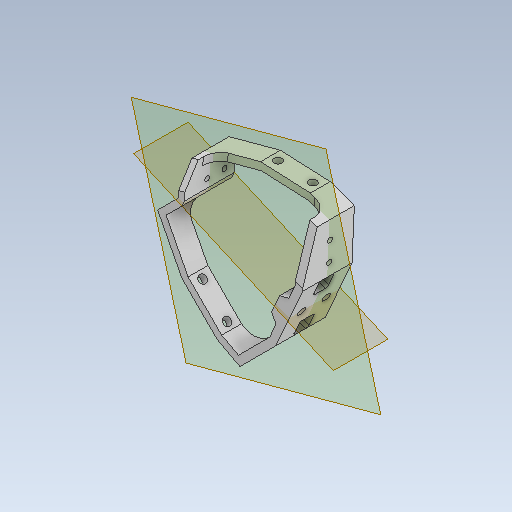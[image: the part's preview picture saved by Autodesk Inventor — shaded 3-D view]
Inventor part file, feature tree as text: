
AUTODESK INVENTOR PART (.ipt)
format: ipt  version: 2020 (Build 240168000, 168)  size: 520,192 bytes
history: native  units: mm
features: sketch x15, reference x15, thicken_offset x14, projected_geometry x13, extrude x11, other x7, plane x4, hole x4, chamfer x4, fillet x2
ambient origin geometry x8: Origin, YZ Plane, XZ Plane, XY Plane, X Axis, Y Axis, Z Axis, Center Point
bodies: Body1 (feature_tree)
feature tree (89):
  sketch  "Sketch1"  dims[d0=3.0mm d1=3.0mm]
  plane  "Work Plane1"
  plane  "Work Plane2"
  extrude  "Extrusion4"  Depth=3.0mm
  hole  "Hole1"  [1 undecoded]
  hole  "Hole2"  [1 undecoded]
  thicken_offset  "Thicken1"
  thicken_offset  "Thicken2"
  extrude  "Extrusion5"  Depth=10.0mm TaperAngle=0.0deg
  hole  "Hole3"  [1 undecoded]
  hole  "Hole4"  [1 undecoded]
  extrude  "Extrusion6"  Depth=2.5mm
  thicken_offset  "Thicken3"
  thicken_offset  "Thicken4"
  extrude  "Extrusion7"  Depth=10.0mm TaperAngle=0.0deg
  extrude  "Extrusion8"  Depth=3.0mm
  thicken_offset  "Thicken5"
  thicken_offset  "Thicken6"
  extrude  "Extrusion9"  Depth=4.0mm
  extrude  "Extrusion10"  Depth=4.0mm
  extrude  "Extrusion11"  Depth=3.0mm
  fillet  "Fillet2"  Radius=3.5mm
  thicken_offset  "Thicken7"
  thicken_offset  "Thicken8"
  chamfer  "Chamfer2"  Distance=1.0mm
  chamfer  "Chamfer3"  Distance=7.0mm
  chamfer  "Chamfer4"  Distance=7.0mm
  chamfer  "Chamfer5"  Distance=4.0mm
  extrude  "Extrusion14"  Depth=4.0mm
  extrude  "Extrusion15"  Depth=1.0mm
  plane  "Work Plane3"
  extrude  "Extrusion16"  Depth=1.0mm
  fillet  "Fillet4"  Radius=3.5mm
  thicken_offset  "Thicken9"
  thicken_offset  "Thicken10"
  thicken_offset  "Thicken11"
  thicken_offset  "Thicken12"
  thicken_offset  "Thicken13"
  thicken_offset  "Thicken14"
  plane  "Work Plane4"
  reference  "Reference1"
  reference  "Reference2"
  sketch  "Sketch4"  dims[d2=3.0mm d3=3.0mm]
  reference  "Reference7"
  reference  "Reference8"
  sketch  "Sketch5"  dims[d4=3.0mm d5=3.0mm]
  reference  "Reference9"
  reference  "Reference10"
  sketch  "Sketch6"  dims[d6=3.0mm d15=10.0mm d16=0.0mm]
  reference  "Reference11"
  reference  "Reference12"
  sketch  "Sketch7"  dims[d17=2.0mm d18=6.0mm d19=4.0mm d20=2.0mm d21=90.0deg d22=5.0mm d23=0.0mm]
  reference  "Reference13"
  reference  "Reference14"
  sketch  "Sketch8"  dims[d24=2.0mm d25=6.0mm d26=4.0mm d27=2.0mm d28=90.0deg d29=5.0mm d30=0.0mm d31=1.0mm]
  reference  "Reference15"
  reference  "Reference16"
  sketch  "Sketch10"  dims[d32=1.0mm d33=1.0mm]
  projected_geometry  "Projected Loop1"
  sketch  "Sketch11"  dims[d34=1.0mm d35=2.5mm]
  projected_geometry  "Projected Loop2"
  projected_geometry  "Projected Loop3"
  reference  "Reference19"
  reference  "Reference20"
  sketch  "Sketch12"  dims[d36=2.5mm d39=10.0mm d40=0.0mm]
  projected_geometry  "Projected Loop4"
  projected_geometry  "Projected Loop5"
  projected_geometry  "Projected Loop6"
  sketch  "Sketch13"  dims[d41=2.0mm d42=6.0mm d43=4.0mm d44=2.0mm d45=90.0deg d46=5.0mm d47=0.0mm]
  projected_geometry  "Projected Loop7"
  projected_geometry  "Projected Loop8"
  reference  "Reference21"
  sketch  "Sketch14"  dims[d48=2.0mm d49=6.0mm d50=4.0mm d51=2.0mm d52=90.0deg d53=5.0mm d54=0.0mm d60=3.0mm]
  projected_geometry  "Projected Loop9"
  sketch  "Sketch15"  dims[d61=4.0mm d62=4.0mm]
  projected_geometry  "Projected Loop10"
  sketch  "Sketch18"  dims[d63=10.0mm d64=0.0mm d65=4.0mm d66=3.0mm]
  projected_geometry  "Projected Loop13"
  sketch  "Sketch19"  dims[d67=4.5mm d68=3.0mm d69=3.5mm d70=3.5mm]
  projected_geometry  "Projected Loop14"
  sketch  "Sketch20"  dims[d71=3.5mm d72=1.0mm d73=7.0mm d74=0.0mm d75=7.0mm d76=0.0mm d79=4.0mm d80=4.0mm d81=4.5mm d82=4.5mm d83=3.5mm d84=3.5mm d85=1.0mm d86=3.5mm d87=7.0mm d88=0.0mm d89=7.0mm d90=0.0mm d91=5.0mm d92=5.0mm d93=3.2mm d94=3.2mm d95=7.0mm d96=0.0mm d100=5.0mm d114=1.0mm d115=1.0mm d116=1.0mm d117=1.0mm d118=5.0mm d119=2.0mm d120=75.0deg d121=5.0mm d122=2.0mm d123=75.0deg d124=5.0mm d125=2.0mm d126=60.0deg d127=5.0mm d128=2.0mm d129=60.0deg d130=7.0mm d131=7.0mm d132=3.2mm d133=3.2mm d134=7.0mm d135=0.0mm d136=7.0mm d137=7.0mm d138=3.2mm d139=3.2mm d140=7.0mm d141=0.0mm d142=7.0mm d143=6.0mm d145=7.0mm d146=6.0mm d147=10.0mm d148=0.0mm d149=1.0mm d150=0.5mm d151=0.5mm d152=0.5mm d153=0.5mm d154=0.5mm d155=0.5mm d156=0.5mm d157=0.5mm d158=0.5mm d159=0.5mm d160=0.5mm d161=0.5mm]
  projected_geometry  "Projected Loop15"
  parser-record x1  (decoder bookkeeping rows leaked as tree rows — omitted from the tree; the rows remain in map.json)
  other  "leg_1.iam"
  other  "reducer_1:1"
  other  "mot_holder_1:1"
  other  "reducer_1:2"
  other  "screw_holder_2_3:6"
  other  "screw_holder_2_3:7"
note: 4 required parameter values undecoded (feature->parameter linkage not recoverable at this tier; creation-order binding heuristic only, values carry confidence <= 0.55)
note: 1 file-system path scrubbed to <path> (originals preserved in map.json)
